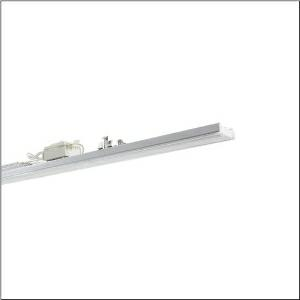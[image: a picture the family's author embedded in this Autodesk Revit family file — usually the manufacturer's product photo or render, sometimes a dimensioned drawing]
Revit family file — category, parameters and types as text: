
# Revit family: licross_r__11_recessed_extreme_mo_51tl12dn4axge_8a86
name_source: partatom
category: Lighting Fixtures
units: mm (PartAtom-declared; Revit-internal decimal feet)

## family parameters
Cut with Voids When Loaded = No
Host = Face
Light Source = No
Part Type = Normal
Room Calculation Point = No
Round Connector Dimension = Use Diameter
Shared = No

## types (1)
- --- (1 x LED, 10240 lm, 56.7 W, 4000K)
    Apparent Load = 57 VA
    CIE Flux Codes = 67 92 99 100 100
    Color Rendering = 80
    Color Temperature = 4000K
    Default Elevation = 1800 mm
    Description = Licross® 11 Recessed extreme MO, luminaire insert, of sheet steel, coil coated, white, length: 1.500mm, width: 66mm, height: 67mm, LED rated luminous flux: 10.240lm, light colour: 840, control gear: DALI 2, with plug, 5-pole, with phase selection, mains connection: 220..240V, AC, 50/60Hz, rated input power: 57W, halogen-free wiring, primary optical cover: cover, of PMMA, light emission: direct distribution, primary light characteristic: symmetric, protection rating (complete): IP40, insulation class (complete): insulation class I (protective earthing), certification: CE, ENEC, VDE, UKCA, protection symbol: D if used in an environment without relevant dust loads with corresponding accessories, impact resistance: IK06, permissible ambient temperature for indoor applications: -40..+45°C, corresponds to IFS (International Featured Standards) requirements for safety and quality in the food industry, reducing of maximum allowable ambient temperature of 5°C with ceiling mounting, LABS conformity tested according to VDMA 24364:2018-05, packaging unit: 1 piece
    Height = 58 mm
    Lamp = 1 x LED
    Lamp Light Flux = 10240 lm
    Lamp Power = 56.7 W
    Lamp count = 1
    Length = 1500 mm
    Luminous efficacy = 181 lm/W
    Manufacturer = Siteco
    ModVariant = No
    Model = 51TL12DN4AXGE
    Mounting Place = Ceiling
    Mounting Type = Pendant
    Number of Poles = 1
    OnlyDefault = Yes
    Power Factor = 1
    Product Name = Licross® 11 Recessed extreme MO
    Product group = luminaire insert
    ProductGroupID = 902
    Protection Class = Protection class I
    Protection Degree = IP 40
    RLX_Detail_Level = 1
    RLX_Emergency_Light_Flux = 0 lm
    RLX_Emergency_Type = 0
    RLX_Emergency_Type_DB = No
    RlxData = <blob elided: 24397 chars, md5=80dc74c8>
    Socket = socket
    Standby Power = 0 W
    System Light Flux = 10240 lm
    System Power = 57 W
    Type Comments = factory setting: luminous flux: 100 % | dim-lin: 254 | 378 mA
    Type Image = l_1296930.jpg
    URL = http://relux.com
    VarID = @adj_082572
    Voltage = 0 V
    Weight = 0.00 kg
    Width = 66 mm

## geometry (parser evidence)
native form markers: Blend x4, Sweep x12
no freeform markers — native parametric forms only
